# Revit family: ROSENBERG_Z_U
name_source: partatom
category: Wyposażenie mechaniczne
revit_build: Autodesk Revit 2016 (Build: 20150714_1515(x64)
units: mm (PartAtom-declared; Revit-internal decimal feet)

## family parameters
Numer OmniClass = 23.75.00.00
Oparty na płaszczyźnie roboczej = Nie
Punkt obliczania pomieszczeń = Nie
Tnij formami wycięć po wczytaniu = Nie
Typ części = Dzieli na
Tytuł OmniClass = Climate Control (HVAC)
Współdzielony = Tak
Wymiar okrągłego złącza = Użyj średnicy
Zawsze pionowo = Tak

## types (1)
- Z 160 U G
    Charakterystyka pracy = https://rosenberg.pl
    Częstotliwość pracy = 50 Hz
    Częstotliwość pracy 1 = 60 Hz
    Klasa szczeloności = IP44
    Masa = 7.50 kg
    Materiał = <Wg kategorii>
    Moc znamionowa = 110 W
    Model = Z  160 U G
    Napięcie znamionowe = 230 V
    Numer katalogowy = F05-16018
    Opis = Wentylator kanałowy Zerobox Ultimate
    Producent = Rosenberg
    Prąd znamionowy = 1 A
    URL = https://rosenberg.pl
    param_Skrzynia długość = 300 mm  [stored 0.984252 ft]
    param_Went.Przył.odsunięcie X = 213 mm  [stored 0.698819 ft]
    param_Went.Przył.odsunięcie Y = 88 mm  [stored 0.288714 ft]
    param_Wentylator długość = 400 mm  [stored 1.31234 ft]
    param_Wentylator szerokość = 300 mm  [stored 0.984252 ft]
    param_Wentylator wysokość = 185 mm  [stored 0.606955 ft]
    param_Wysokość kołnierza = 30 mm  [stored 0.0984252 ft]
    param_b1 = 100 mm  [stored 0.328084 ft]
    param_f1 = 267 mm
    param_otwor.sr = 145 mm  [stored 0.475722 ft]
    param_ramie = 105 mm  [stored 0.344488 ft]
    Średnica przyłącza = 160 mm  [stored 0.524934 ft]

note: [stored X ft] marks values corroborated as IEEE doubles in the binary element streams (Revit-internal decimal feet)

## geometry (parser evidence)
native form markers: Blend x2, Sweep x3
no freeform markers — native parametric forms only
